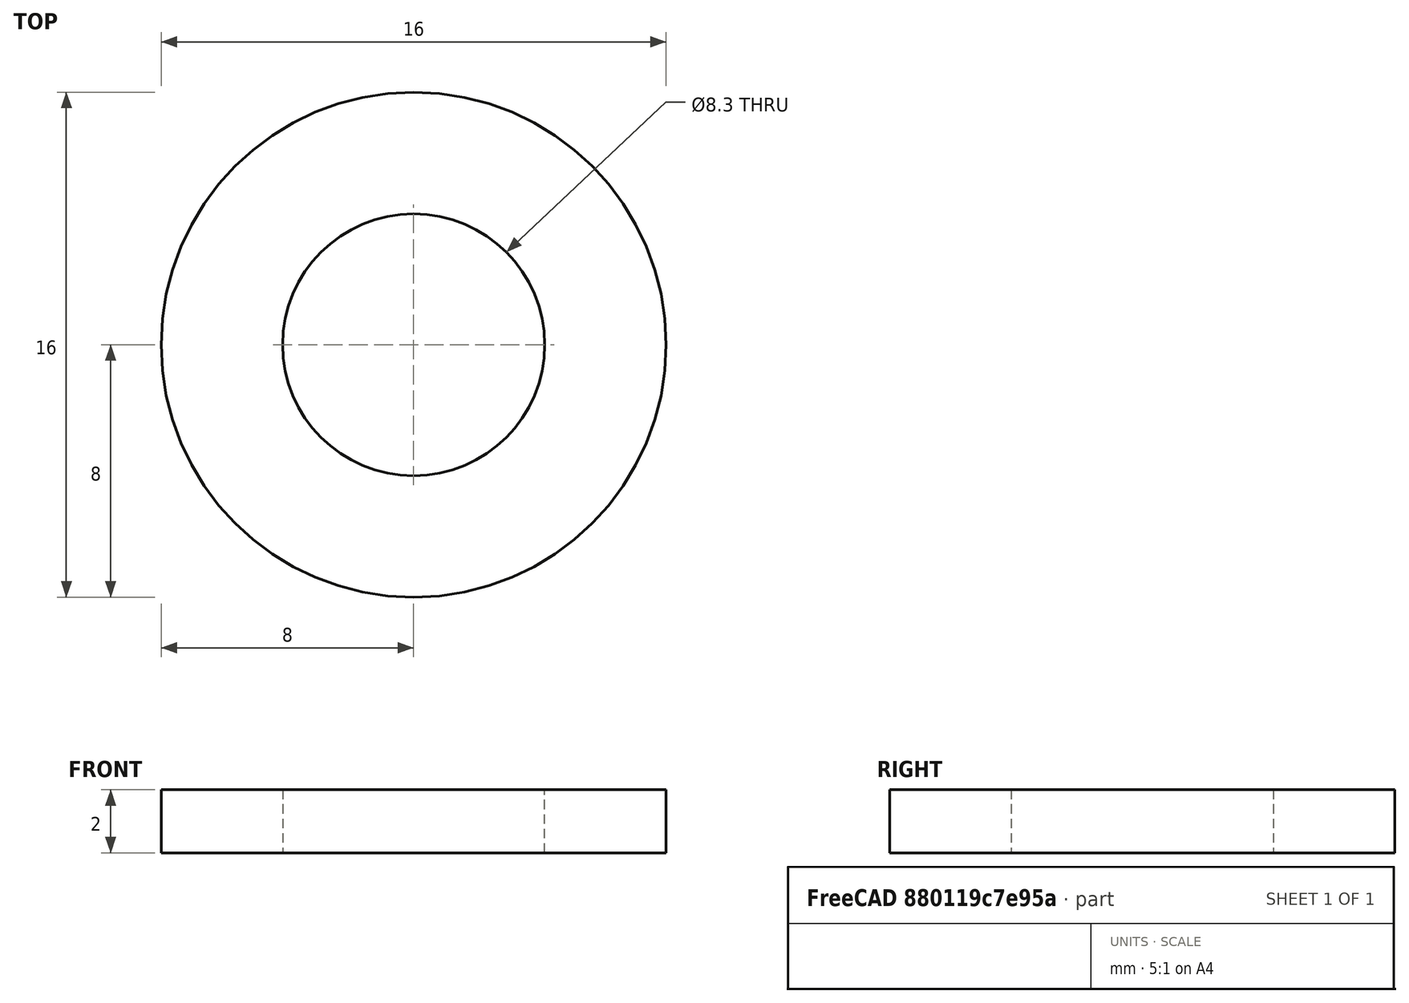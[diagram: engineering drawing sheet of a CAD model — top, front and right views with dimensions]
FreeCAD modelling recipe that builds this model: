
FCSTD DOCUMENT  (FreeCAD 0.19R17089 +1543 (Git))
Label: project-document
License: All rights reserved
LicenseURL: http://en.wikipedia.org/wiki/All_rights_reserved
objects: App::FeaturePython×2, Part::FeaturePython×2, Sketcher::SketchObject×1, PartDesign::Pad×1, PartDesign::Body×1
note: 5 computed .brp shape members not serialized (recipe doc carries the construction recipe); baked Part::Feature solids carry a one-line shape summary decoded from their .brp

FEATURE [Sketcher::SketchObject] Sketch
  MapMode = 5
  Support = -> [XY_Plane]
  sketch-geometry (2):
    g0: Circle CenterX=0 CenterY=0 CenterZ=0 NormalX=0 NormalY=0 NormalZ=1 AngleXU=0 Radius=4.15
    g1: Circle CenterX=0 CenterY=0 CenterZ=0 NormalX=0 NormalY=0 NormalZ=1 AngleXU=0 Radius=8
  constraints (4):
    c: Coincident(g0,g-1)
    c: Coincident(g1,g0)
    c: Diameter(g0) = 8.3  'D1'
    c: Diameter(g1) = 16  'D2'
FEATURE [PartDesign::Pad] Pad
  ClaimChildren = false
  Length = 2
  Length2 = 100
  Profile = -> Sketch
  Type = 0
FEATURE [PartDesign::Body] Body
  Group = -> [Sketch,Pad]
  Origin = -> Origin
  Tip = -> Pad
FEATURE [App::FeaturePython] Constraints  # WARN: FeaturePython — macro-defined, semantics opaque (R4)
  GroupMode = 1
  _Version = 1
FEATURE [App::FeaturePython] Elements  # WARN: FeaturePython — macro-defined, semantics opaque (R4)
  GroupMode = 1
FEATURE [Part::FeaturePython] Parts  # WARN: FeaturePython — macro-defined, semantics opaque (R4)
  Group = -> [Body]
  GroupMode = 0
FEATURE [Part::FeaturePython] Assembly  label="Washer 000"  # WARN: FeaturePython — macro-defined, semantics opaque (R4)
  AutoRelax = true
  BuildShape = 0
  Freeze = false
  Group = -> [Constraints,Elements,Parts]
  GroupMode = 1
  SolverType = 1
  Verbose = false
  _SolverType = 1
  _Version = 1
